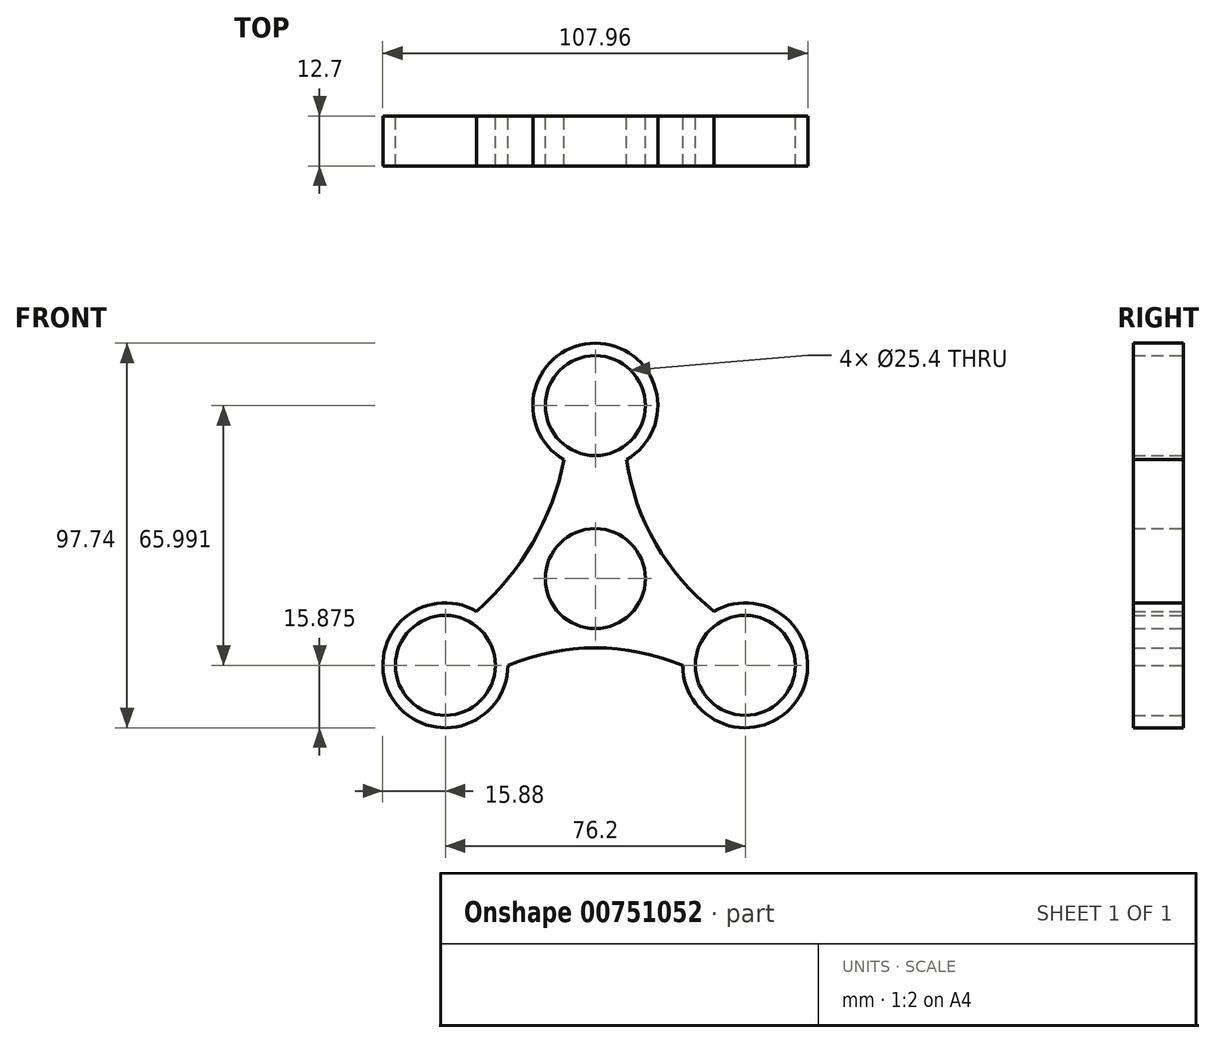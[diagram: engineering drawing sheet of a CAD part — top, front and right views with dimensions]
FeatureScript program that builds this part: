
annotation { "Feature Type Name" : "Feature", "Feature Type Description" : "" }
export const myFeature = defineFeature(function(context is Context, id is Id, definition is map)
    precondition{}
    {
        {
            var Q0;
            Q0=qCreatedBy(makeId("Front.planeOp"),FACE);
            var sketch = newSketch(context, id + "F0", { "sketchPlane" : qUnion([Q0])});
            skCircle(sketch, "E0", {"center": v(0, 44.37) * mm, "radius": 15.88 * mm});
            skCircle(sketch, "E1", {"center": v(38.1, -21.62) * mm, "radius": 15.88 * mm});
            skCircle(sketch, "E2", {"center": v(-38.1, -21.62) * mm, "radius": 15.88 * mm});
            skCircle(sketch, "E3", {"center": v(0, 0.4) * mm, "radius": 15.73 * mm});
            skPoint(sketch, "E4.third.point", {"position": v(30.16, -7.88) * mm});
            skArc(sketch, "E5", {"start": v(7.94, 30.62) * mm, "mid": v(15.37, 9.25) * mm, "end": v(30.16, -7.88) * mm});
            skArc(sketch, "E6", {"start": v(22.22, -21.62) * mm, "mid": v(0, -17.2) * mm, "end": v(-22.23, -21.62) * mm});
            skArc(sketch, "E7", {"start": v(-30.16, -7.88) * mm, "mid": v(-15.87, 9.54) * mm, "end": v(-7.94, 30.62) * mm});
            skSolve(sketch);
        }
        {
            var Q0;
            {var subQ0=sQuery(id+"F0.wireOp",EDGE,"E2");var subQ1=makeQuery(id+"F0.imprint","INTERSECT",VERTEX,{"derivedFrom":[subQ0,sQuery(id+"F0.wireOp",EDGE,"E6")]});Q0=makeQuery(id+"F0.imprint","IMPRINT",FACE,{"disambiguationData":[TD([[makeQuery(id+"F0.imprint","IMPRINT",EDGE,{"disambiguationData":[TD([[subQ1,-1.0]])],"derivedFrom":subQ0}),1.0]])]});}
            var Q1;
            Q1=makeQuery(id+"F0.imprint","IMPRINT",FACE,{"disambiguationData":[TD([[makeQuery(id+"F0.imprint","IMPRINT",EDGE,{"derivedFrom":sQuery(id+"F0.wireOp",EDGE,"E3")}),-1.0]])]});
            var Q2;
            {var subQ0=sQuery(id+"F0.wireOp",EDGE,"E1");var subQ1=makeQuery(id+"F0.imprint","INTERSECT",VERTEX,{"derivedFrom":[subQ0,sQuery(id+"F0.wireOp",EDGE,"E5")]});Q2=makeQuery(id+"F0.imprint","IMPRINT",FACE,{"disambiguationData":[TD([[makeQuery(id+"F0.imprint","IMPRINT",EDGE,{"disambiguationData":[TD([[subQ1,-1.0]])],"derivedFrom":subQ0}),1.0]])]});}
            var Q3;
            Q3=makeQuery(id+"F0.imprint","IMPRINT",FACE,{"disambiguationData":[TD([[makeQuery(id+"F0.imprint","IMPRINT",EDGE,{"derivedFrom":sQuery(id+"F0.wireOp",EDGE,"E3")}),1.0]])]});
            var Q4;
            {var subQ0=sQuery(id+"F0.wireOp",EDGE,"E0");var subQ1=makeQuery(id+"F0.imprint","INTERSECT",VERTEX,{"derivedFrom":[subQ0,sQuery(id+"F0.wireOp",EDGE,"E5")]});Q4=makeQuery(id+"F0.imprint","IMPRINT",FACE,{"disambiguationData":[TD([[makeQuery(id+"F0.imprint","IMPRINT",EDGE,{"disambiguationData":[TD([[subQ1,1.0]])],"derivedFrom":subQ0}),1.0]])]});}
            extrude(context, id + "F1", {"entities" : qUnion([Q0, Q1, Q2, Q3, Q4]), "depth" : 12.7 * mm, "offsetDistance" : 25.4 * mm});
        }
        {
            var Q0;
            Q0=sQuery(id+"F0.wireOp",VERTEX,"E2.center");
            var Q1;
            Q1=sQuery(id+"F0.wireOp",VERTEX,"E1.center");
            var Q2;
            Q2=sQuery(id+"F0.wireOp",VERTEX,"E0.center");
            var Q3;
            Q3=sQuery(id+"F0.wireOp",VERTEX,"E3.center");
            var Q4;
            Q4=makeQuery(id+"F1.opExtrude","SWEPT_BODY",BODY,{"disambiguationData":[OSD([sQuery(id+"F0.wireOp",EDGE,"E0"),sQuery(id+"F0.wireOp",EDGE,"E1"),sQuery(id+"F0.wireOp",EDGE,"E2"),sQuery(id+"F0.wireOp",EDGE,"E5"),sQuery(id+"F0.wireOp",EDGE,"E6"),sQuery(id+"F0.wireOp",EDGE,"E7")])]});
            hole(context, id + "F2", {"style" : HoleStyle.SIMPLE, "endStyle" : HoleEndStyle.THROUGH, "oppositeDirection" : true, "holeDiameter" : 25.4 * mm, "majorDiameter" : 6.35 * mm, "isTappedThrough" : true, "tappedDepth" : 12.7 * mm, "tapClearance" : 3, "locations" : qUnion([Q0, Q1, Q2, Q3]), "scope" : qUnion([Q4])});
        }
    });
